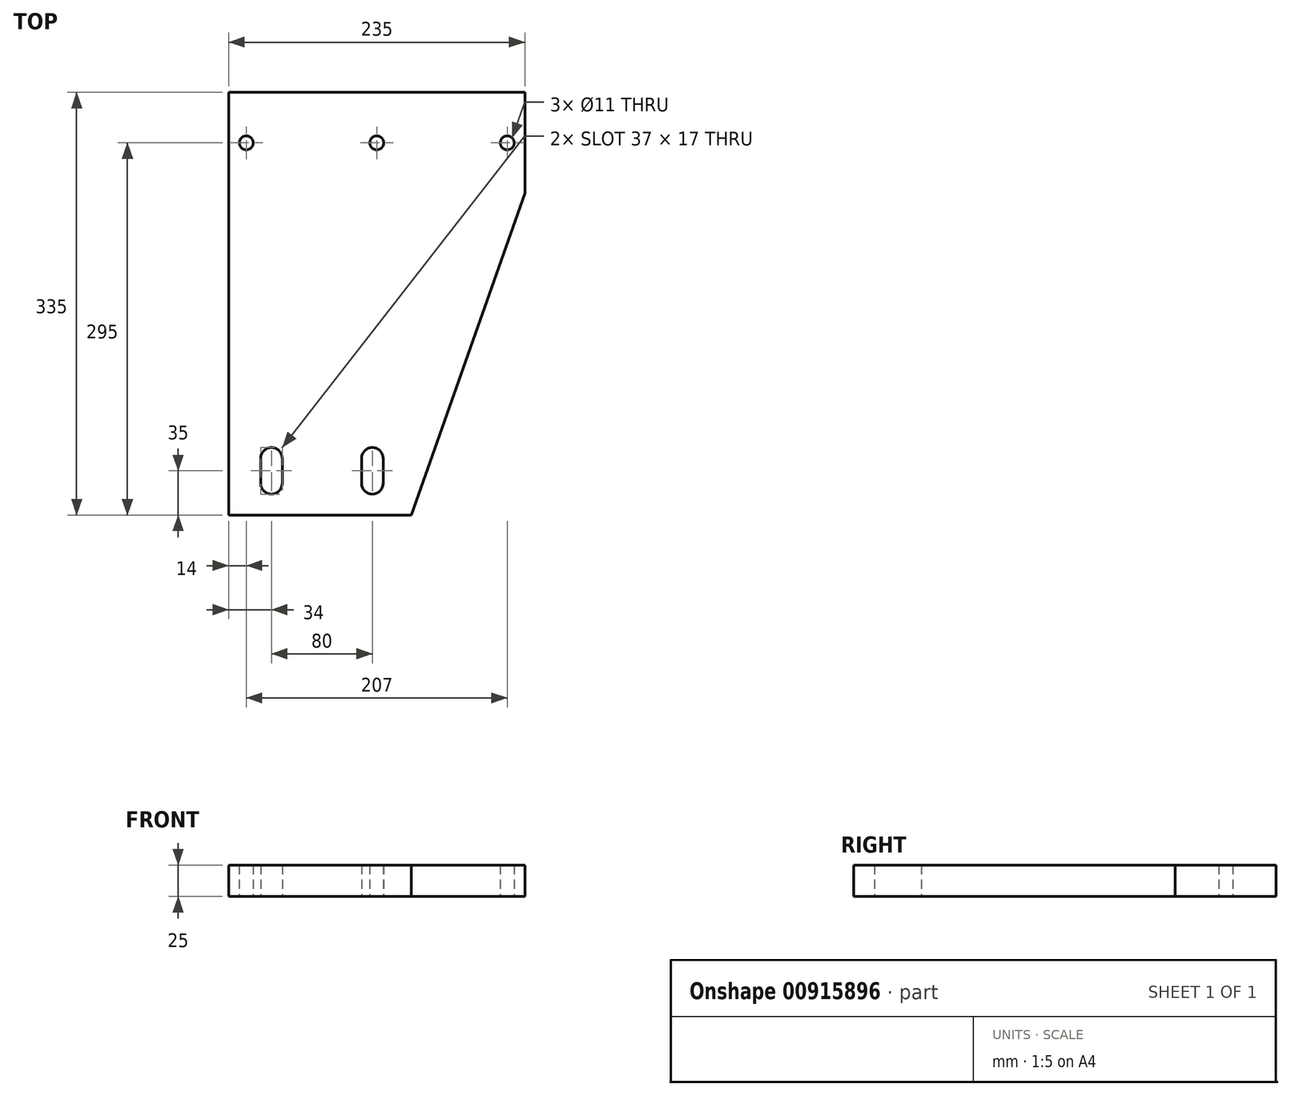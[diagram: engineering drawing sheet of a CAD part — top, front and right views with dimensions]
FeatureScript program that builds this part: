
annotation { "Feature Type Name" : "Feature", "Feature Type Description" : "" }
export const myFeature = defineFeature(function(context is Context, id is Id, definition is map)
    precondition{}
    {
        {
            var Q0;
            Q0=qCreatedBy(makeId("Top.planeOp"),FACE);
            var sketch = newSketch(context, id + "F0", { "sketchPlane" : qUnion([Q0])});
            skLineSegment(sketch, "E0", {"start": v(-235, 80) * mm, "end": v(-235, -255) * mm});
            skLineSegment(sketch, "E1", {"start": v(-235, 80) * mm, "end": v(0, 80) * mm});
            skLineSegment(sketch, "E2", {"start": v(0, 80) * mm, "end": v(0, 0) * mm});
            skLineSegment(sketch, "E3", {"start": v(-235, -255) * mm, "end": v(-90, -255) * mm});
            skLineSegment(sketch, "E4", {"start": v(0, 0) * mm, "end": v(-90, -255) * mm});
            skCircle(sketch, "E5", {"center": v(-221, 40) * mm, "radius": 5.5 * mm});
            skCircle(sketch, "E6", {"center": v(-117.5, 40) * mm, "radius": 5.5 * mm});
            skCircle(sketch, "E7", {"center": v(-14, 40) * mm, "radius": 5.5 * mm});
            skArc(sketch, "E8", {"start": v(-192.5, -210) * mm, "mid": v(-201, -201.5) * mm, "end": v(-209.5, -210) * mm});
            skArc(sketch, "E9", {"start": v(-209.5, -230) * mm, "mid": v(-201, -238.5) * mm, "end": v(-192.5, -230) * mm});
            skLineSegment(sketch, "E10", {"start": v(-209.5, -210) * mm, "end": v(-209.5, -230) * mm});
            skLineSegment(sketch, "E11", {"start": v(-192.5, -210) * mm, "end": v(-192.5, -230) * mm});
            skArc(sketch, "E12", {"start": v(-112.5, -210) * mm, "mid": v(-121, -201.5) * mm, "end": v(-129.5, -210) * mm});
            skArc(sketch, "E13", {"start": v(-129.5, -230) * mm, "mid": v(-121, -238.5) * mm, "end": v(-112.5, -230) * mm});
            skLineSegment(sketch, "E14", {"start": v(-129.5, -210) * mm, "end": v(-129.5, -230) * mm});
            skLineSegment(sketch, "E15", {"start": v(-112.5, -210) * mm, "end": v(-112.5, -230) * mm});
            skSolve(sketch);
        }
        {
            var Q0;
            Q0 = qSketchRegion(id + "F0", true);
            extrude(context, id + "F1", {"entities" : qUnion([Q0]), "depth" : 25 * mm, "offsetDistance" : 25 * mm});
        }
        {
            var Q0;
            Q0 = qSketchRegion(id + "F0", true);
            extrude(context, id + "F2", {"entities" : qUnion([Q0]), "operationType" : NewBodyOperationType.ADD, "depth" : 25 * mm, "offsetDistance" : 25 * mm});
        }
    });
